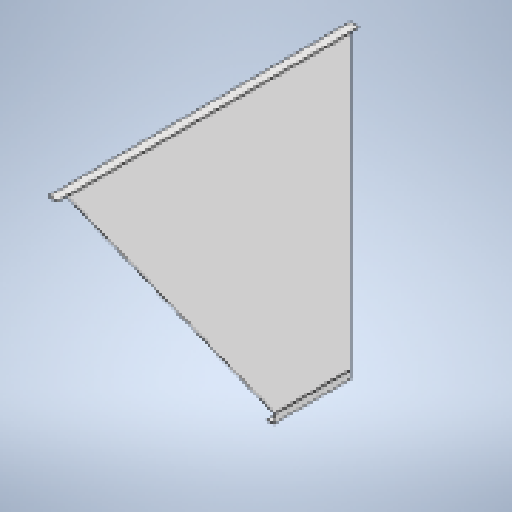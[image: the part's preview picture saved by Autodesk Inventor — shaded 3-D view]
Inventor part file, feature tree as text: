
AUTODESK INVENTOR PART (.ipt)
format: ipt  version: 2025.1 (Build 291241020, 241B)  size: 313,856 bytes
history: native  units: mm
features: sheet_metal_op x9, other x5, sketch x5, extrude x2, projected_geometry x2, mirror x1
ambient origin geometry x8: Origin, YZ Plane, XZ Plane, XY Plane, X Axis, Y Axis, Z Axis, Center Point
bodies: Body1 (feature_tree)
feature tree (24):
  sheet_metal_op  "Contour Flange2"
  other  "A-Side Definition"
  extrude  "Extrusion14"  Depth=200.0mm
  mirror  "Mirror1"
  extrude  "Extrusion15"  TaperAngle=0.0deg  [1 undecoded]
  sheet_metal_op  "Flange3"
  sheet_metal_op  "Flange4"
  sketch  "Sketch1"  dims[d0=1000.0mm d61=200.0mm]
  other  "Plate4"
  sheet_metal_op  "Bend4"
  sheet_metal_op  "Corner4"
  sketch  "Sketch20"  dims[d66=5.0mm d68=0.0mm]
  projected_geometry  "Projected Loop12"
  sketch  "Sketch21"  dims[d69=3.0mm]
  projected_geometry  "Projected Loop13"
  sketch  "Sketch22"  dims[d70=3.0mm]
  other  "Plate5"
  sheet_metal_op  "Bend5"
  sheet_metal_op  "Corner5"
  sketch  "Sketch23"  dims[d71=1.5mm d72=6.0mm d73=5.0mm d74=1500.0mm d75=5.0mm d76=4.0mm d77=12.0mm d78=3.0mm d79=5.0mm d87=20.666414mm d90=50.0mm d114=50.0mm d115=0.0mm d116=20.736395mm d117=2.0mm d118=2.0mm d119=11.200136mm d120=0.0mm d121=0.0mm d122=400.0mm d123=750.0mm d124=3.0mm d125=1.5mm d126=6.0mm d127=5.0mm d128=50.0mm d129=5.028432mm d130=5.0mm d131=12.0mm d132=3.0mm d133=5.0mm d134=3.0mm d135=1.5mm d136=6.0mm d137=5.0mm d138=40.0mm d139=90.0deg d140=5.0mm d141=12.0mm d142=3.0mm d143=5.0mm]
  other  "Plate6"
  sheet_metal_op  "Bend6"
  sheet_metal_op  "Corner6"
  other  "Definition1"
note: 1 required parameter value undecoded (feature->parameter linkage not recoverable at this tier; creation-order binding heuristic only, values carry confidence <= 0.55)
